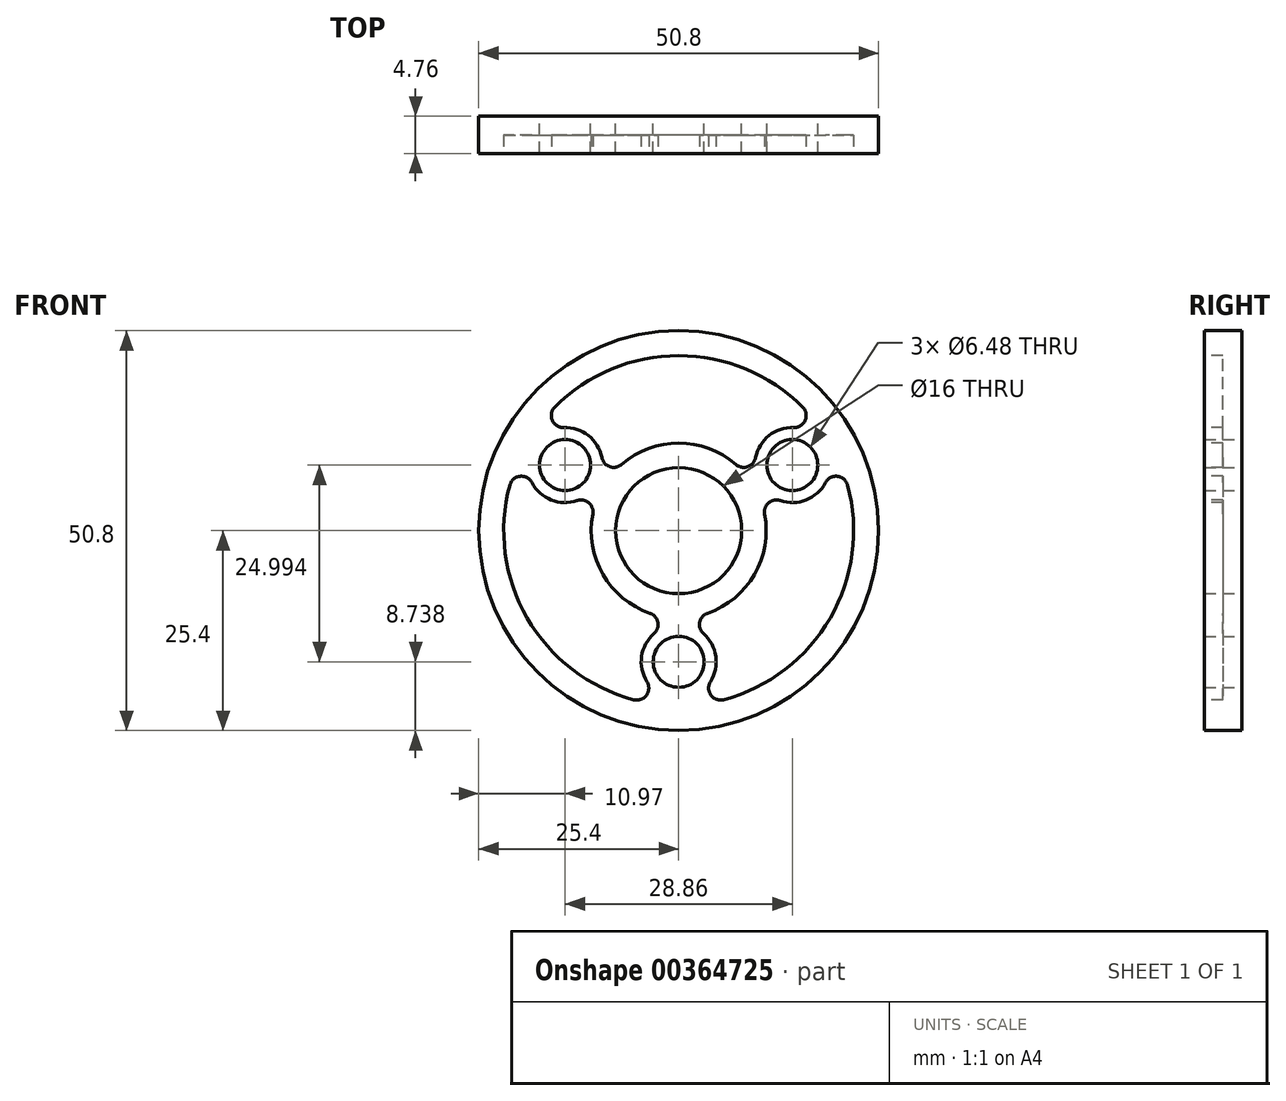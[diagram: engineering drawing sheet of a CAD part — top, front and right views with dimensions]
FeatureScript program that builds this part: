
annotation { "Feature Type Name" : "Feature", "Feature Type Description" : "" }
export const myFeature = defineFeature(function(context is Context, id is Id, definition is map)
    precondition{}
    {
        {
            var Q0;
            Q0=qCreatedBy(makeId("Front.planeOp"),FACE);
            var sketch = newSketch(context, id + "F0", { "sketchPlane" : qUnion([Q0])});
            skCircle(sketch, "E0", {"center": v(0, 0) * mm, "radius": 16.66 * mm, "construction": true});
            skCircle(sketch, "E1", {"center": v(-14.43, 8.33) * mm, "radius": 3.24 * mm});
            skCircle(sketch, "E2", {"center": v(14.43, 8.33) * mm, "radius": 3.24 * mm});
            skCircle(sketch, "E3", {"center": v(0, -16.66) * mm, "radius": 3.24 * mm});
            skCircle(sketch, "E4", {"center": v(0, 0) * mm, "radius": 25.4 * mm});
            skCircle(sketch, "E5", {"center": v(0, 0) * mm, "radius": 8 * mm});
            skLineSegment(sketch, "E6", {"start": v(-14.43, 8.33) * mm, "end": v(0, -16.66) * mm, "construction": true});
            skLineSegment(sketch, "E7", {"start": v(14.43, 8.33) * mm, "end": v(0, -16.66) * mm, "construction": true});
            skLineSegment(sketch, "E8", {"start": v(14.43, 8.33) * mm, "end": v(-14.43, 8.33) * mm, "construction": true});
            skSolve(sketch);
        }
        {
            var Q0;
            Q0=qSketchRegion(id+"F0",true);
            extrude(context, id + "F1", {"entities" : qUnion([Q0]), "depth" : 4.76 * mm});
        }
        {
            var Q0;
            Q0=makeQuery(id+"F1.opExtrude","CAP_FACE",FACE,{"disambiguationData":[OSD([sQuery(id+"F0.wireOp",EDGE,"E1"),sQuery(id+"F0.wireOp",EDGE,"E2"),sQuery(id+"F0.wireOp",EDGE,"E3"),sQuery(id+"F0.wireOp",EDGE,"E4"),sQuery(id+"F0.wireOp",EDGE,"E5")])],"isStart":false});
            var sketch = newSketch(context, id + "F2", { "sketchPlane" : qUnion([Q0])});
            skArc(sketch, "E9", {"start": v(-10.91, 2.1) * mm, "mid": v(-9.62, -5.56) * mm, "end": v(-3.65, -10.5) * mm});
            skArc(sketch, "E10", {"start": v(7.27, 8.4) * mm, "mid": v(0, 11.11) * mm, "end": v(-7.27, 8.4) * mm});
            skArc(sketch, "E11", {"start": v(3.65, -10.5) * mm, "mid": v(9.62, -5.56) * mm, "end": v(10.91, 2.1) * mm});
            skArc(sketch, "E12", {"start": v(-9.76, 9.26) * mm, "mid": v(-11.48, 12.07) * mm, "end": v(-14.6, 13.1) * mm});
            skArc(sketch, "E13", {"start": v(-18.64, 6.1) * mm, "mid": v(-16.2, 3.9) * mm, "end": v(-12.9, 3.82) * mm});
            skArc(sketch, "E14", {"start": v(-21.46, 5.79) * mm, "mid": v(-19.25, -11.11) * mm, "end": v(-5.72, -21.48) * mm});
            skArc(sketch, "E15", {"start": v(5.72, -21.48) * mm, "mid": v(19.25, -11.11) * mm, "end": v(21.46, 5.79) * mm});
            skArc(sketch, "E16.filletArc", {"start": v(-10.91, 2.1) * mm, "mid": v(-11.4, 3.53) * mm, "end": v(-12.9, 3.82) * mm});
            skArc(sketch, "E17.filletArc", {"start": v(-18.64, 6.1) * mm, "mid": v(-20.16, 6.9) * mm, "end": v(-21.46, 5.79) * mm});
            skArc(sketch, "E18.filletArc", {"start": v(-9.76, 9.26) * mm, "mid": v(-8.76, 8.12) * mm, "end": v(-7.27, 8.4) * mm});
            skArc(sketch, "E19", {"start": v(12.9, 3.82) * mm, "mid": v(16.2, 3.9) * mm, "end": v(18.64, 6.1) * mm});
            skArc(sketch, "E20", {"start": v(14.6, 13.1) * mm, "mid": v(11.48, 12.07) * mm, "end": v(9.76, 9.26) * mm});
            skArc(sketch, "E21", {"start": v(4.03, -19.2) * mm, "mid": v(4.71, -15.97) * mm, "end": v(3.14, -13.08) * mm});
            skArc(sketch, "E22", {"start": v(-3.14, -13.08) * mm, "mid": v(-4.71, -15.97) * mm, "end": v(-4.03, -19.2) * mm});
            skArc(sketch, "E23.filletArc", {"start": v(-5.72, -21.48) * mm, "mid": v(-4.1, -20.9) * mm, "end": v(-4.03, -19.2) * mm});
            skArc(sketch, "E24.filletArc", {"start": v(-3.14, -13.08) * mm, "mid": v(-2.65, -11.64) * mm, "end": v(-3.65, -10.5) * mm});
            skArc(sketch, "E25.filletArc", {"start": v(4.03, -19.2) * mm, "mid": v(4.1, -20.9) * mm, "end": v(5.72, -21.48) * mm});
            skArc(sketch, "E26.filletArc", {"start": v(3.65, -10.5) * mm, "mid": v(2.65, -11.64) * mm, "end": v(3.14, -13.08) * mm});
            skArc(sketch, "E27.filletArc", {"start": v(21.46, 5.79) * mm, "mid": v(20.16, 6.9) * mm, "end": v(18.64, 6.1) * mm});
            skArc(sketch, "E28.filletArc", {"start": v(12.9, 3.82) * mm, "mid": v(11.4, 3.53) * mm, "end": v(10.91, 2.1) * mm});
            skArc(sketch, "E29.filletArc", {"start": v(7.27, 8.4) * mm, "mid": v(8.76, 8.12) * mm, "end": v(9.76, 9.26) * mm});
            skArc(sketch, "E30", {"start": v(15.74, 15.69) * mm, "mid": v(0, 22.23) * mm, "end": v(-15.74, 15.69) * mm});
            skArc(sketch, "E31.filletArc", {"start": v(-15.74, 15.69) * mm, "mid": v(-16.06, 14) * mm, "end": v(-14.6, 13.1) * mm});
            skArc(sketch, "E32.filletArc", {"start": v(14.6, 13.1) * mm, "mid": v(16.06, 14) * mm, "end": v(15.74, 15.69) * mm});
            skSolve(sketch);
        }
        {
            var Q0;
            Q0=qSketchRegion(id+"F2",true);
            extrude(context, id + "F3", {"entities" : qUnion([Q0]), "operationType" : NewBodyOperationType.REMOVE, "oppositeDirection" : true, "depth" : 2.38 * mm, "offsetDistance" : 25.4 * mm});
        }
    });
